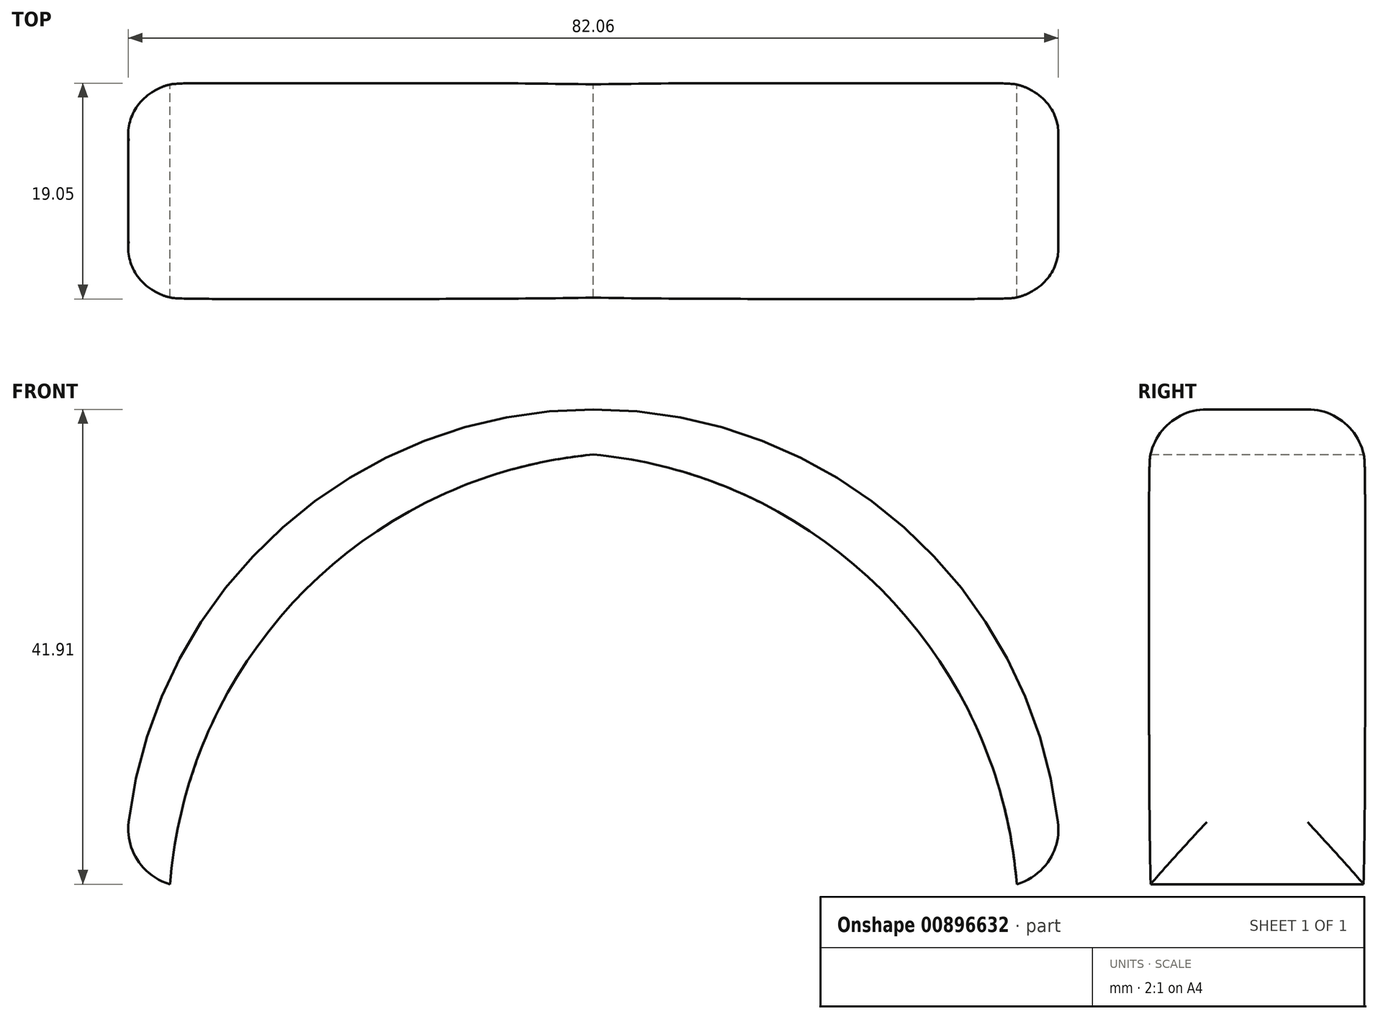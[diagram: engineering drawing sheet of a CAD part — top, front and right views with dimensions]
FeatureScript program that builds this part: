
annotation { "Feature Type Name" : "Feature", "Feature Type Description" : "" }
export const myFeature = defineFeature(function(context is Context, id is Id, definition is map)
    precondition{}
    {
        {
            var Q0;
            Q0=qCreatedBy(makeId("Front.planeOp"),FACE);
            var sketch = newSketch(context, id + "F0", { "sketchPlane" : qUnion([Q0])});
            skArc(sketch, "E0", {"start": v(41.28, 8.89) * mm, "mid": v(29.41, 38.49) * mm, "end": v(0, 50.8) * mm});
            skArc(sketch, "E1", {"start": v(37.35, 8.89) * mm, "mid": v(25.6, 34.67) * mm, "end": v(0, 46.81) * mm});
            skLineSegment(sketch, "E2", {"start": v(41.28, 8.89) * mm, "end": v(37.35, 8.89) * mm});
            skArc(sketch, "E3.MirrorCS", {"start": v(-41.27, 8.89) * mm, "mid": v(-29.41, 38.49) * mm, "end": v(0, 50.8) * mm});
            skArc(sketch, "E4.MirrorCS", {"start": v(-37.35, 8.89) * mm, "mid": v(-25.6, 34.67) * mm, "end": v(0, 46.81) * mm});
            skLineSegment(sketch, "E5.MirrorCS", {"start": v(-41.27, 8.89) * mm, "end": v(-37.35, 8.89) * mm});
            skSolve(sketch);
        }
        {
            var Q0;
            Q0=makeQuery(id+"F0.imprint","IMPRINT",FACE,{"disambiguationData":[TD([[makeQuery(id+"F0.imprint","IMPRINT",EDGE,{"derivedFrom":sQuery(id+"F0.wireOp",EDGE,"E0")}),1.0]])]});
            extrude(context, id + "F1", {"entities" : qUnion([Q0]), "depth" : 19.05 * mm, "offsetDistance" : 25.4 * mm});
        }
        {
            var Q0;
            Q0=makeQuery(id+"F1.opExtrude","SWEPT_EDGE",EDGE,{"disambiguationData":[OSD([sQuery(id+"F0.wireOp",EDGE,"E0"),sQuery(id+"F0.wireOp",EDGE,"E2")])]});
            var Q1;
            Q1=makeQuery(id+"F1.opExtrude","CAP_EDGE",EDGE,{"disambiguationData":[OSD([sQuery(id+"F0.wireOp",EDGE,"E0"),sQuery(id+"F0.wireOp",EDGE,"E3.MirrorCS")])],"isStart":true});
            var Q2;
            Q2=makeQuery(id+"F1.opExtrude","CAP_EDGE",EDGE,{"disambiguationData":[OSD([sQuery(id+"F0.wireOp",EDGE,"E0"),sQuery(id+"F0.wireOp",EDGE,"E3.MirrorCS")])],"isStart":false});
            var Q3;
            Q3=makeQuery(id+"F1.opExtrude","SWEPT_EDGE",EDGE,{"disambiguationData":[OSD([sQuery(id+"F0.wireOp",EDGE,"E3.MirrorCS"),sQuery(id+"F0.wireOp",EDGE,"E5.MirrorCS")])]});
            fillet(context, id + "F2", {"entities" : qUnion([Q0, Q1, Q2, Q3]), "radius" : 5.08 * mm, "tangentPropagation" : true, "allowEdgeOverflow" : false});
        }
    });
